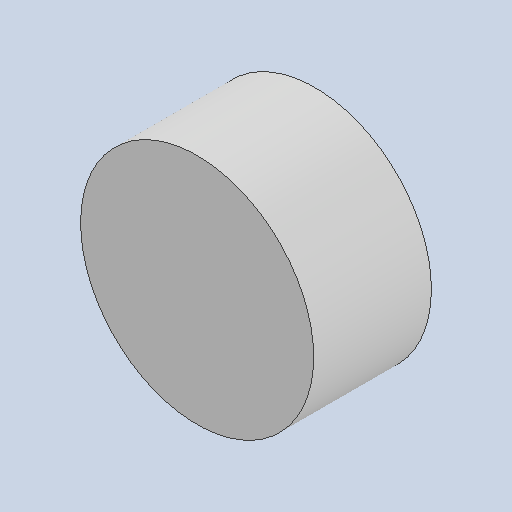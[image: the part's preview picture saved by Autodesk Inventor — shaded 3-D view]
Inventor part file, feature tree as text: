
AUTODESK INVENTOR PART (.ipt)
format: ipt  version: 2022 (Build 260153070, 153G)  size: 95,744 bytes
history: native  units: mm
features: reference x4, other x3, sketch x1, plane x1, extrude x1
ambient origin geometry x8: Origin, YZ Plane, XZ Plane, XY Plane, X Axis, Y Axis, Z Axis, Center Point
bodies: Solid1 (feature_tree)
feature tree (10):
  sketch  "Sketch1"  dims[d0=2.0mm d6=0.15mm d7=0.15mm d8=10.0mm d9=0.0mm]
  plane  "Work Plane1"
  extrude  "Extrusion1"  Depth=10.0mm
  reference  "Reference1"
  reference  "Reference2"
  reference  "Reference3"
  reference  "Reference4"
  other  "<userpath> laptop\Desktop\SumoBot\sumobotENCODER\MotorEncoderAssembly.iam"
  other  "MotorEncoderAssembly.iam"
  other  "TT motor output:1"
